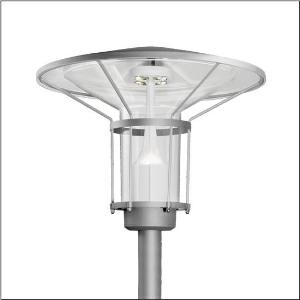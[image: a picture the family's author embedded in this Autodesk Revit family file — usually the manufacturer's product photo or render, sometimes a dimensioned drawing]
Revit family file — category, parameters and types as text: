
# Revit family: laterne_classic_iq___p1_0a_5xa5245bf14h_da05
name_source: partatom
category: Lighting Fixtures
units: mm (PartAtom-declared; Revit-internal decimal feet)

## family parameters
Cut with Voids When Loaded = No
Host = Face
Light Source = No
Part Type = Normal
Room Calculation Point = No
Round Connector Dimension = Use Diameter
Shared = No

## types (1)
- --- (1 x LED, 1360 lm, 12.9 W, 2200K)
    Apparent Load = 13 VA
    CIE Flux Codes = 30 61 91 96 100
    Color Rendering = 70
    Color Temperature = 2200K
    Default Elevation = 1800 mm
    Description = Lantern Classic iQ, mast luminaire, Module 540 iQ-SR, primary light control with 3 zone facetted reflector, of plastic, silver coated, highly specular, structured, primary optical cover: cover, of PMMA, transparent, light distribution: P1.0a, light emission: direct distribution, primary light characteristic: strongly asymmetric, installation type: post-top, LED, High Power LED, rated luminous flux: 1.360lm, luminous efficacy: 105lm/W, light colour: 722, colour temperature: 2200K, control gear: ECG iQ, control: presetting dimming logarithmic, Street-Remote, Auto-Match, Temp-Guard, Lumen-Switch, Night-Set, Smart-Wire, Light-Fading, Desk-Remote (wireless, voltage-free reading and setting of iQ features in the workshop via application-optimized NFC function/RFID function), optimised constant luminous flux control (CLO 2.0), with terminal, 6-pole, max. 2.5mm², mains connection: 230..240V, AC, 50/60Hz, start of lifetime: 13W, end of service life: 13W, reduction: 6W, luminaire housing, upper part, of glass-fibre reinforced polyester, coated, Siteco® metallic grey (DB 702S), diameter: 750mm, height: 596mm, spigot size: d x l = 76 x 70mm (post-top) | with reducer (optional accessory) 60 x 70mm, post-top mast mounting element, of diecast aluminium, coated, Siteco® metallic grey (DB 702S), Module 540 iQ-SR, traffic white (RAL 9016), equipment: standard, protection rating (complete): IP65, insulation class (complete): insulation class II (safety insulation), certification: CE, ENEC, VDE, packaging unit: 1 piece

Light Distribution: P1.0a
    Height = 596 mm
    Lamp = 1 x LED
    Lamp Light Flux = 1360 lm
    Lamp Power = 12.9 W
    Lamp count = 1
    Length = 750 mm
    Luminous efficacy = 105 lm/W
    Manufacturer = Siteco
    ModVariant = No
    Model = 5XA5245BF14H
    Number of Poles = 1
    OnlyDefault = Yes
    Power Factor = 1
    Product Name = Laterne Classic iQ | P1.0a
    Product group = mast luminaire | pylon top
    ProductGroupID = 6100
    Protection Class = Protection class II
    Protection Degree = IP 65
    RLX_Detail_Level = 1
    RLX_Emergency_Light_Flux = 0 lm
    RLX_Emergency_Type = 0
    RLX_Emergency_Type_DB = No
    RlxData = <blob elided: 94461 chars, md5=315010e0>
    Socket = socket
    Standby Power = 0 W
    System Light Flux = 1360 lm
    System Power = 13 W
    Type Comments = factory setting: luminous flux: 100 % | dim-lin: 254 | 516 mA
    Type Image = l_1006052.jpg
    URL = http://relux.com
    VarID = @adj_110453
    Voltage = 0 V
    Weight = 0.00 kg
    Width = 0 mm  [stored 0 ft]

note: [stored X ft] marks values corroborated as IEEE doubles in the binary element streams (Revit-internal decimal feet)

## geometry (parser evidence)
native form markers: Blend x4, Sweep x10
no freeform markers — native parametric forms only
